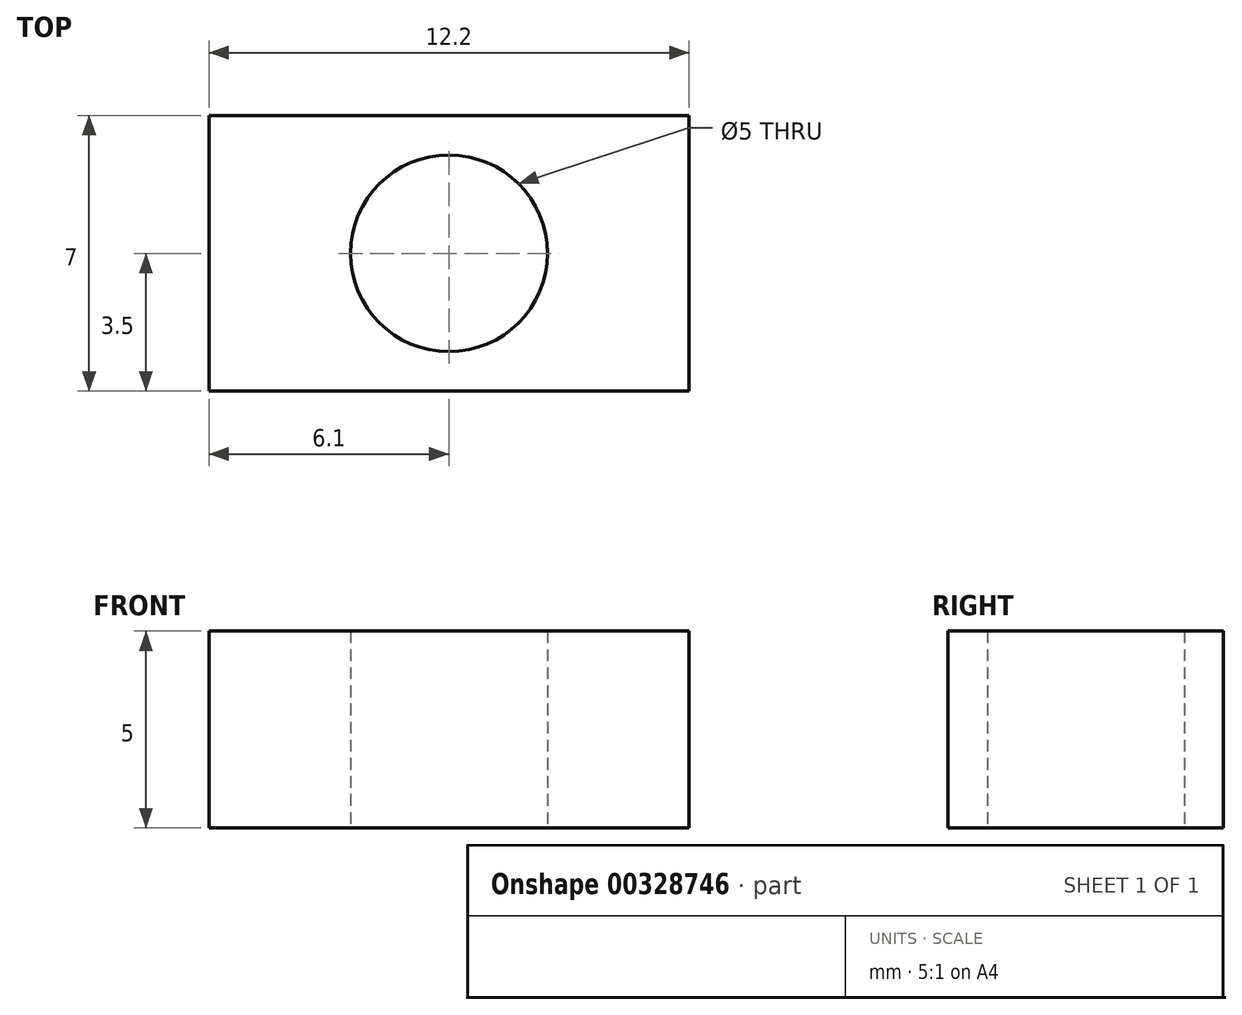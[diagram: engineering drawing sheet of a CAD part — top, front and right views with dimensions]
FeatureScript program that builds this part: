
annotation { "Feature Type Name" : "Feature", "Feature Type Description" : "" }
export const myFeature = defineFeature(function(context is Context, id is Id, definition is map)
    precondition{}
    {
        {
            var Q0;
            Q0=qCreatedBy(makeId("Top.planeOp"),FACE);
            var sketch = newSketch(context, id + "F0", { "sketchPlane" : qUnion([Q0])});
            skLineSegment(sketch, "E0.bottom", {"start": v(-6.1, 3.5) * mm, "end": v(6.1, 3.5) * mm});
            skLineSegment(sketch, "E0.top", {"start": v(-6.1, -3.5) * mm, "end": v(6.1, -3.5) * mm});
            skLineSegment(sketch, "E0.left", {"start": v(-6.1, 3.5) * mm, "end": v(-6.1, -3.5) * mm});
            skLineSegment(sketch, "E0.right", {"start": v(6.1, 3.5) * mm, "end": v(6.1, -3.5) * mm});
            skLineSegment(sketch, "E1", {"start": v(-6.1, 3.5) * mm, "end": v(6.1, -3.5) * mm, "construction": true});
            skCircle(sketch, "E2", {"center": v(0, 0) * mm, "radius": 2.5 * mm});
            skSolve(sketch);
        }
        {
            var Q0;
            Q0 = qSketchRegion(id + "F0", true);
            extrude(context, id + "F1", {"entities" : qUnion([Q0]), "depth" : 5 * mm});
        }
    });
